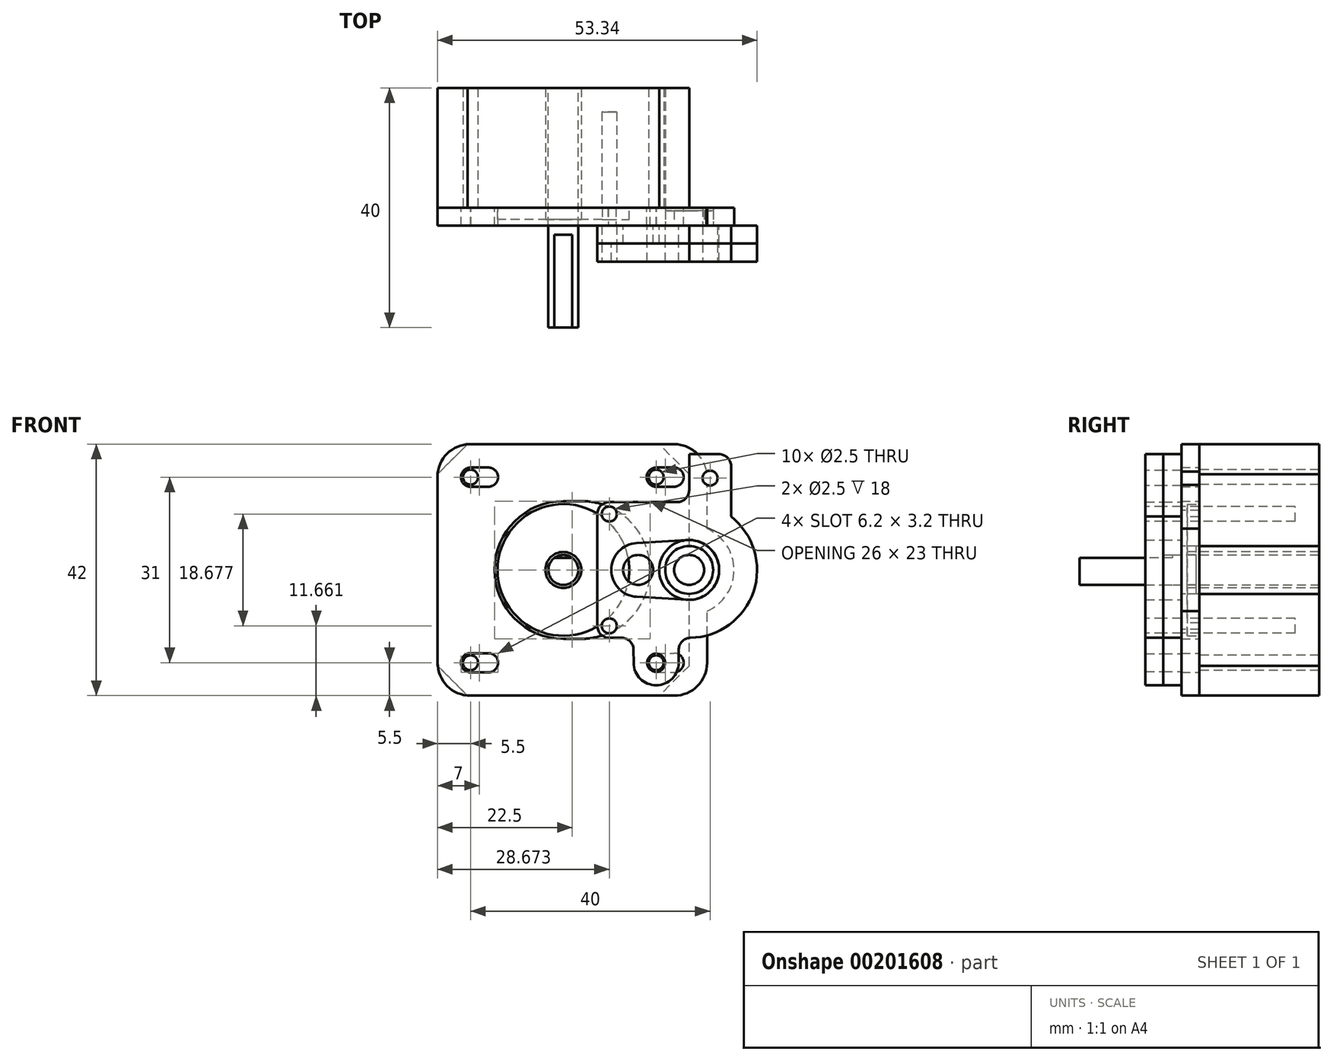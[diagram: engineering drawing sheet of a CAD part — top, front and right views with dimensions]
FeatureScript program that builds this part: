
annotation { "Feature Type Name" : "Feature", "Feature Type Description" : "" }
export const myFeature = defineFeature(function(context is Context, id is Id, definition is map)
    precondition{}
    {
        {
            var Q0;
            Q0=qCreatedBy(makeId("Front.planeOp"),FACE);
            var sketch = newSketch(context, id + "F0", { "sketchPlane" : qUnion([Q0])});
            skCircle(sketch, "E0", {"center": v(0, 0) * mm, "radius": 11 * mm});
            skCircle(sketch, "E1", {"center": v(0, 0) * mm, "radius": 3 * mm});
            skLineSegment(sketch, "E2.bottom", {"start": v(21, -21) * mm, "end": v(-21, -21) * mm});
            skLineSegment(sketch, "E2.top", {"start": v(21, 21) * mm, "end": v(-21, 21) * mm});
            skLineSegment(sketch, "E2.left", {"start": v(21, -21) * mm, "end": v(21, 21) * mm});
            skLineSegment(sketch, "E2.right", {"start": v(-21, -21) * mm, "end": v(-21, 21) * mm});
            skLineSegment(sketch, "E3.bottom", {"start": v(15.5, -15.5) * mm, "end": v(-15.5, -15.5) * mm, "construction": true});
            skLineSegment(sketch, "E3.top", {"start": v(15.5, 15.5) * mm, "end": v(-15.5, 15.5) * mm, "construction": true});
            skLineSegment(sketch, "E3.left", {"start": v(15.5, -15.5) * mm, "end": v(15.5, 15.5) * mm, "construction": true});
            skLineSegment(sketch, "E3.right", {"start": v(-15.5, -15.5) * mm, "end": v(-15.5, 15.5) * mm, "construction": true});
            skCircle(sketch, "E4", {"center": v(-15.5, 15.5) * mm, "radius": 1.25 * mm});
            skCircle(sketch, "E5", {"center": v(15.5, 15.5) * mm, "radius": 1.25 * mm});
            skCircle(sketch, "E6", {"center": v(15.5, -15.5) * mm, "radius": 1.25 * mm});
            skCircle(sketch, "E7", {"center": v(-15.5, -15.5) * mm, "radius": 1.25 * mm});
            skSolve(sketch);
        }
        {
            var Q0;
            Q0 = qSketchRegion(id + "F0", true);
            var Q1;
            Q1=makeQuery(id+"F0.imprint","IMPRINT",FACE,{"disambiguationData":[TD([[makeQuery(id+"F0.imprint","IMPRINT",EDGE,{"derivedFrom":sQuery(id+"F0.wireOp",EDGE,"E0")}),1.0]])]});
            extrude(context, id + "F1", {"entities" : qUnion([Q0, Q1]), "oppositeDirection" : true, "depth" : 20 * mm});
        }
        {
            var Q0;
            Q0=makeQuery(id+"F0.imprint","IMPRINT",FACE,{"disambiguationData":[TD([[makeQuery(id+"F0.imprint","IMPRINT",EDGE,{"derivedFrom":sQuery(id+"F0.wireOp",EDGE,"E0")}),1.0]])]});
            extrude(context, id + "F2", {"entities" : qUnion([Q0]), "operationType" : NewBodyOperationType.ADD, "depth" : 2 * mm});
        }
        {
            var Q0;
            Q0=makeQuery(id+"F1.opExtrude","SWEPT_EDGE",EDGE,{"disambiguationData":[OSD([sQuery(id+"F0.wireOp",EDGE,"E2.top"),sQuery(id+"F0.wireOp",EDGE,"E2.right")])]});
            var Q1;
            Q1=makeQuery(id+"F1.opExtrude","SWEPT_EDGE",EDGE,{"disambiguationData":[OSD([sQuery(id+"F0.wireOp",EDGE,"E2.top"),sQuery(id+"F0.wireOp",EDGE,"E2.left")])]});
            var Q2;
            Q2=makeQuery(id+"F1.opExtrude","SWEPT_EDGE",EDGE,{"disambiguationData":[OSD([sQuery(id+"F0.wireOp",EDGE,"E2.bottom"),sQuery(id+"F0.wireOp",EDGE,"E2.left")])]});
            var Q3;
            Q3=makeQuery(id+"F1.opExtrude","SWEPT_EDGE",EDGE,{"disambiguationData":[OSD([sQuery(id+"F0.wireOp",EDGE,"E2.bottom"),sQuery(id+"F0.wireOp",EDGE,"E2.right")])]});
            chamfer(context, id + "F3", {"entities" : qUnion([Q0, Q1, Q2, Q3]), "width" : 5 * mm, "tangentPropagation" : true});
        }
        {
            var Q0;
            Q0=makeQuery(id+"F1.opExtrude","CAP_FACE",FACE,{"disambiguationData":[OSD([sQuery(id+"F0.wireOp",EDGE,"E1"),sQuery(id+"F0.wireOp",EDGE,"E2.bottom"),sQuery(id+"F0.wireOp",EDGE,"E2.top"),sQuery(id+"F0.wireOp",EDGE,"E2.left"),sQuery(id+"F0.wireOp",EDGE,"E2.right"),sQuery(id+"F0.wireOp",EDGE,"E4"),sQuery(id+"F0.wireOp",EDGE,"E5"),sQuery(id+"F0.wireOp",EDGE,"E6"),sQuery(id+"F0.wireOp",EDGE,"E7")])],"isStart":false});
            var sketch = newSketch(context, id + "F4", { "sketchPlane" : qUnion([Q0])});
            skCircle(sketch, "E8", {"center": v(0, 0) * mm, "radius": 2.5 * mm});
            skSolve(sketch);
        }
        {
            var Q0;
            Q0 = qSketchRegion(id + "F4", true);
            extrude(context, id + "F5", {"entities" : qUnion([Q0]), "oppositeDirection" : true, "depth" : 40 * mm});
        }
        {
            var Q0;
            Q0=makeQuery(id+"F5.opExtrude","CAP_FACE",FACE,{"disambiguationData":[OSD([sQuery(id+"F4.wireOp",EDGE,"E8")])],"isStart":false});
            var sketch = newSketch(context, id + "F6", { "sketchPlane" : qUnion([Q0])});
            skLineSegment(sketch, "E9", {"start": v(-6.96, 2) * mm, "end": v(7.74, 2) * mm});
            skSolve(sketch);
        }
        {
            var Q0;
            {var subQ0=sQuery(id+"F6.wireOp",EDGE,"E9");var subQ1=makeQuery(id+"F5.opExtrude","CAP_EDGE",EDGE,{"disambiguationData":[OSD([sQuery(id+"F4.wireOp",EDGE,"E8")])],"isStart":false});var subQ2=makeQuery(id+"F6.imprint","INTERSECT",VERTEX,{"disambiguationData":[OD(0.0)],"derivedFrom":[subQ1,subQ0]});Q0=makeQuery(id+"F6.imprint","IMPRINT",FACE,{"disambiguationData":[TD([[makeQuery(id+"F6.imprint","IMPRINT",EDGE,{"disambiguationData":[TD([[subQ2,-1.0]])],"derivedFrom":subQ0}),1.0]])]});}
            extrude(context, id + "F7", {"entities" : qUnion([Q0]), "operationType" : NewBodyOperationType.REMOVE, "oppositeDirection" : true, "depth" : 15.5 * mm});
        }
        {
            var Q0;
            Q0=makeQuery(id+"F1.opExtrude","CAP_FACE",FACE,{"disambiguationData":[OSD([sQuery(id+"F0.wireOp",EDGE,"E1"),sQuery(id+"F0.wireOp",EDGE,"E2.bottom"),sQuery(id+"F0.wireOp",EDGE,"E2.top"),sQuery(id+"F0.wireOp",EDGE,"E2.left"),sQuery(id+"F0.wireOp",EDGE,"E2.right"),sQuery(id+"F0.wireOp",EDGE,"E4"),sQuery(id+"F0.wireOp",EDGE,"E5"),sQuery(id+"F0.wireOp",EDGE,"E6"),sQuery(id+"F0.wireOp",EDGE,"E7")])],"isStart":true});
            var sketch = newSketch(context, id + "F8", { "sketchPlane" : qUnion([Q0])});
            skArc(sketch, "E10", {"start": v(-15.48, 17.1) * mm, "mid": v(-17.1, 15.47) * mm, "end": v(-15.41, 13.9) * mm});
            skLineSegment(sketch, "E11", {"start": v(-15.5, 15.5) * mm, "end": v(-10.86, 15.5) * mm, "construction": true});
            skLineSegment(sketch, "E12", {"start": v(0, 0) * mm, "end": v(16.5, 0) * mm, "construction": true});
            skArc(sketch, "E13", {"start": v(-12.5, 13.9) * mm, "mid": v(-10.9, 15.5) * mm, "end": v(-12.5, 17.1) * mm});
            skArc(sketch, "E14", {"start": v(3, -11.5) * mm, "mid": v(14.5, 0) * mm, "end": v(3, 11.5) * mm});
            skLineSegment(sketch, "E15", {"start": v(-15.52, 17.1) * mm, "end": v(-12.5, 17.1) * mm});
            skLineSegment(sketch, "E16", {"start": v(-15.41, 13.9) * mm, "end": v(-12.5, 13.9) * mm});
            skLineSegment(sketch, "E17", {"start": v(0, 11.5) * mm, "end": v(3, 11.5) * mm});
            skLineSegment(sketch, "E18", {"start": v(0, -11.5) * mm, "end": v(3, -11.5) * mm});
            skArc(sketch, "E19.trimOffspring", {"start": v(0, 11.5) * mm, "mid": v(-11.5, 0) * mm, "end": v(0, -11.5) * mm});
            skLineSegment(sketch, "E20.0.1.0", {"start": v(-15.5, -15.5) * mm, "end": v(-10.86, -15.5) * mm, "construction": true});
            skArc(sketch, "E20.0.1.1", {"start": v(-15.48, -13.9) * mm, "mid": v(-17.1, -15.53) * mm, "end": v(-15.41, -17.1) * mm});
            skLineSegment(sketch, "E20.0.1.2", {"start": v(-15.41, -17.1) * mm, "end": v(-12.5, -17.1) * mm});
            skArc(sketch, "E20.0.1.3", {"start": v(-12.5, -17.1) * mm, "mid": v(-10.9, -15.5) * mm, "end": v(-12.5, -13.9) * mm});
            skLineSegment(sketch, "E20.0.1.4", {"start": v(-15.52, -13.9) * mm, "end": v(-12.5, -13.9) * mm});
            skLineSegment(sketch, "E20.1.0.0", {"start": v(15.5, 15.5) * mm, "end": v(20.14, 15.5) * mm, "construction": true});
            skArc(sketch, "E20.1.0.1", {"start": v(15.52, 17.1) * mm, "mid": v(13.9, 15.47) * mm, "end": v(15.59, 13.9) * mm});
            skLineSegment(sketch, "E20.1.0.2", {"start": v(15.59, 13.9) * mm, "end": v(18.5, 13.9) * mm});
            skArc(sketch, "E20.1.0.3", {"start": v(18.5, 13.9) * mm, "mid": v(20.1, 15.5) * mm, "end": v(18.5, 17.1) * mm});
            skLineSegment(sketch, "E20.1.0.4", {"start": v(15.48, 17.1) * mm, "end": v(18.5, 17.1) * mm});
            skLineSegment(sketch, "E20.1.1.0", {"start": v(15.5, -15.5) * mm, "end": v(20.14, -15.5) * mm, "construction": true});
            skArc(sketch, "E20.1.1.1", {"start": v(15.52, -13.9) * mm, "mid": v(13.9, -15.53) * mm, "end": v(15.59, -17.1) * mm});
            skLineSegment(sketch, "E20.1.1.2", {"start": v(15.59, -17.1) * mm, "end": v(18.5, -17.1) * mm});
            skArc(sketch, "E20.1.1.3", {"start": v(18.5, -17.1) * mm, "mid": v(20.1, -15.5) * mm, "end": v(18.5, -13.9) * mm});
            skLineSegment(sketch, "E20.1.1.4", {"start": v(15.48, -13.9) * mm, "end": v(18.5, -13.9) * mm});
            skLineSegment(sketch, "E20.direction1", {"start": v(-15.41, 13.9) * mm, "end": v(15.59, 13.9) * mm, "construction": true});
            skLineSegment(sketch, "E20.direction2", {"start": v(-15.41, 13.9) * mm, "end": v(-15.41, -17.1) * mm, "construction": true});
            skLineSegment(sketch, "E21.bottom", {"start": v(18.5, -21) * mm, "end": v(-15.5, -21) * mm});
            skLineSegment(sketch, "E21.top", {"start": v(18.5, 21) * mm, "end": v(-15.6, 21) * mm});
            skLineSegment(sketch, "E21.left", {"start": v(24, -15.5) * mm, "end": v(24, -6.87) * mm});
            skLineSegment(sketch, "E22", {"start": v(-21, -15.5) * mm, "end": v(-21, 15.6) * mm});
            skPoint(sketch, "E23.orphan", {"position": v(-21, 0) * mm});
            skPoint(sketch, "E21.right.end.orphan", {"position": v(-24, 21) * mm});
            skPoint(sketch, "E21.right.start.orphan", {"position": v(-24, -21) * mm});
            skLineSegment(sketch, "E24.trimOffspring", {"start": v(24, 6.87) * mm, "end": v(24, 15.5) * mm});
            skPoint(sketch, "E25.visualSharp", {"position": v(24, 21) * mm});
            skArc(sketch, "E25.filletArc", {"start": v(24, 15.5) * mm, "mid": v(22.39, 19.39) * mm, "end": v(18.5, 21) * mm});
            skPoint(sketch, "E26.visualSharp", {"position": v(-21, 21) * mm});
            skArc(sketch, "E26.filletArc", {"start": v(-15.6, 21) * mm, "mid": v(-19.42, 19.42) * mm, "end": v(-21, 15.6) * mm});
            skPoint(sketch, "E27.visualSharp", {"position": v(-21, -21) * mm});
            skArc(sketch, "E27.filletArc", {"start": v(-21, -15.5) * mm, "mid": v(-19.39, -19.39) * mm, "end": v(-15.5, -21) * mm});
            skPoint(sketch, "E28.visualSharp", {"position": v(24, -21) * mm});
            skArc(sketch, "E28.filletArc", {"start": v(18.5, -21) * mm, "mid": v(22.39, -19.39) * mm, "end": v(24, -15.5) * mm});
            skArc(sketch, "E29", {"start": v(24, -6.87) * mm, "mid": v(28.5, 0) * mm, "end": v(24, 6.87) * mm});
            skSolve(sketch);
        }
        {
            var Q0;
            Q0 = qSketchRegion(id + "F8", true);
            extrude(context, id + "F9", {"entities" : qUnion([Q0]), "depth" : 3 * mm});
        }
        {
            var Q0;
            Q0=makeQuery(id+"F9.opExtrude","CAP_FACE",FACE,{"disambiguationData":[OSD([sQuery(id+"F8.wireOp",EDGE,"E10"),sQuery(id+"F8.wireOp",EDGE,"E13"),sQuery(id+"F8.wireOp",EDGE,"E14"),sQuery(id+"F8.wireOp",EDGE,"E15"),sQuery(id+"F8.wireOp",EDGE,"E16"),sQuery(id+"F8.wireOp",EDGE,"E17"),sQuery(id+"F8.wireOp",EDGE,"E18"),sQuery(id+"F8.wireOp",EDGE,"E19.trimOffspring"),sQuery(id+"F8.wireOp",EDGE,"E20.0.1.1"),sQuery(id+"F8.wireOp",EDGE,"E20.0.1.2"),sQuery(id+"F8.wireOp",EDGE,"E20.0.1.3"),sQuery(id+"F8.wireOp",EDGE,"E20.0.1.4"),sQuery(id+"F8.wireOp",EDGE,"E20.1.0.1"),sQuery(id+"F8.wireOp",EDGE,"E20.1.0.2"),sQuery(id+"F8.wireOp",EDGE,"E20.1.0.3"),sQuery(id+"F8.wireOp",EDGE,"E20.1.0.4"),sQuery(id+"F8.wireOp",EDGE,"E20.1.1.1"),sQuery(id+"F8.wireOp",EDGE,"E20.1.1.2"),sQuery(id+"F8.wireOp",EDGE,"E20.1.1.3"),sQuery(id+"F8.wireOp",EDGE,"E20.1.1.4"),sQuery(id+"F8.wireOp",EDGE,"E21.bottom"),sQuery(id+"F8.wireOp",EDGE,"E21.top"),sQuery(id+"F8.wireOp",EDGE,"E21.left"),sQuery(id+"F8.wireOp",EDGE,"E22")])],"isStart":false});
            var sketch = newSketch(context, id + "F10", { "sketchPlane" : qUnion([Q0])});
            skPoint(sketch, "E30.endSnap0", {"position": v(24, -11.19) * mm});
            skLineSegment(sketch, "E31", {"start": v(0, 0) * mm, "end": v(21, 0) * mm, "construction": true});
            skCircle(sketch, "E32", {"center": v(21, 0) * mm, "radius": 4 * mm});
            skSolve(sketch);
        }
        {
            var Q0;
            Q0=makeQuery(id+"F10.imprint","IMPRINT",FACE,{"disambiguationData":[TD([[makeQuery(id+"F10.imprint","IMPRINT",EDGE,{"derivedFrom":sQuery(id+"F10.wireOp",EDGE,"E32")}),1.0]])]});
            extrude(context, id + "F11", {"entities" : qUnion([Q0]), "operationType" : NewBodyOperationType.REMOVE, "oppositeDirection" : true, "depth" : 25 * mm});
        }
        {
            var Q0;
            Q0=makeQuery(id+"F9.opExtrude","CAP_FACE",FACE,{"disambiguationData":[OSD([sQuery(id+"F8.wireOp",EDGE,"E10"),sQuery(id+"F8.wireOp",EDGE,"E13"),sQuery(id+"F8.wireOp",EDGE,"E14"),sQuery(id+"F8.wireOp",EDGE,"E15"),sQuery(id+"F8.wireOp",EDGE,"E16"),sQuery(id+"F8.wireOp",EDGE,"E17"),sQuery(id+"F8.wireOp",EDGE,"E18"),sQuery(id+"F8.wireOp",EDGE,"E19.trimOffspring"),sQuery(id+"F8.wireOp",EDGE,"E20.0.1.1"),sQuery(id+"F8.wireOp",EDGE,"E20.0.1.2"),sQuery(id+"F8.wireOp",EDGE,"E20.0.1.3"),sQuery(id+"F8.wireOp",EDGE,"E20.0.1.4"),sQuery(id+"F8.wireOp",EDGE,"E20.1.0.1"),sQuery(id+"F8.wireOp",EDGE,"E20.1.0.2"),sQuery(id+"F8.wireOp",EDGE,"E20.1.0.3"),sQuery(id+"F8.wireOp",EDGE,"E20.1.0.4"),sQuery(id+"F8.wireOp",EDGE,"E20.1.1.1"),sQuery(id+"F8.wireOp",EDGE,"E20.1.1.2"),sQuery(id+"F8.wireOp",EDGE,"E20.1.1.3"),sQuery(id+"F8.wireOp",EDGE,"E20.1.1.4"),sQuery(id+"F8.wireOp",EDGE,"E21.bottom"),sQuery(id+"F8.wireOp",EDGE,"E21.top"),sQuery(id+"F8.wireOp",EDGE,"E21.left"),sQuery(id+"F8.wireOp",EDGE,"E22"),sQuery(id+"F8.wireOp",EDGE,"E24.trimOffspring"),sQuery(id+"F8.wireOp",EDGE,"E25.filletArc"),sQuery(id+"F8.wireOp",EDGE,"E26.filletArc"),sQuery(id+"F8.wireOp",EDGE,"E27.filletArc"),sQuery(id+"F8.wireOp",EDGE,"E28.filletArc"),sQuery(id+"F8.wireOp",EDGE,"E29")])],"isStart":false});
            var sketch = newSketch(context, id + "F12", { "sketchPlane" : qUnion([Q0])});
            skCircle(sketch, "E33", {"center": v(21, 0) * mm, "radius": 4 * mm});
            skCircle(sketch, "E34", {"center": v(21, 0) * mm, "radius": 2.5 * mm});
            skSolve(sketch);
        }
        {
            var Q0;
            Q0=makeQuery(id+"F12.imprint","IMPRINT",FACE,{"disambiguationData":[TD([[makeQuery(id+"F12.imprint","IMPRINT",EDGE,{"derivedFrom":sQuery(id+"F12.wireOp",EDGE,"E33")}),1.0]])]});
            extrude(context, id + "F13", {"entities" : qUnion([Q0]), "oppositeDirection" : true, "depth" : 2.5 * mm});
        }
        {
            var Q0;
            Q0=makeQuery(id+"F9.opExtrude","CAP_FACE",FACE,{"disambiguationData":[OSD([sQuery(id+"F8.wireOp",EDGE,"E10"),sQuery(id+"F8.wireOp",EDGE,"E13"),sQuery(id+"F8.wireOp",EDGE,"E14"),sQuery(id+"F8.wireOp",EDGE,"E15"),sQuery(id+"F8.wireOp",EDGE,"E16"),sQuery(id+"F8.wireOp",EDGE,"E17"),sQuery(id+"F8.wireOp",EDGE,"E18"),sQuery(id+"F8.wireOp",EDGE,"E19.trimOffspring"),sQuery(id+"F8.wireOp",EDGE,"E20.0.1.1"),sQuery(id+"F8.wireOp",EDGE,"E20.0.1.2"),sQuery(id+"F8.wireOp",EDGE,"E20.0.1.3"),sQuery(id+"F8.wireOp",EDGE,"E20.0.1.4"),sQuery(id+"F8.wireOp",EDGE,"E20.1.0.1"),sQuery(id+"F8.wireOp",EDGE,"E20.1.0.2"),sQuery(id+"F8.wireOp",EDGE,"E20.1.0.3"),sQuery(id+"F8.wireOp",EDGE,"E20.1.0.4"),sQuery(id+"F8.wireOp",EDGE,"E20.1.1.1"),sQuery(id+"F8.wireOp",EDGE,"E20.1.1.2"),sQuery(id+"F8.wireOp",EDGE,"E20.1.1.3"),sQuery(id+"F8.wireOp",EDGE,"E20.1.1.4"),sQuery(id+"F8.wireOp",EDGE,"E21.bottom"),sQuery(id+"F8.wireOp",EDGE,"E21.top"),sQuery(id+"F8.wireOp",EDGE,"E21.left"),sQuery(id+"F8.wireOp",EDGE,"E22"),sQuery(id+"F8.wireOp",EDGE,"E24.trimOffspring"),sQuery(id+"F8.wireOp",EDGE,"E25.filletArc"),sQuery(id+"F8.wireOp",EDGE,"E26.filletArc"),sQuery(id+"F8.wireOp",EDGE,"E27.filletArc"),sQuery(id+"F8.wireOp",EDGE,"E28.filletArc"),sQuery(id+"F8.wireOp",EDGE,"E29")])],"isStart":false});
            var sketch = newSketch(context, id + "F14", { "sketchPlane" : qUnion([Q0])});
            skLineSegment(sketch, "E35.right", {"start": v(5.67, -9.34) * mm, "end": v(5.67, 9.34) * mm});
            skPoint(sketch, "E35.middle", {"position": v(21, 0) * mm});
            skLineSegment(sketch, "E36.right", {"start": v(19.26, -15.5) * mm, "end": v(19.26, -13.34) * mm});
            skLineSegment(sketch, "E37.trimOffspring", {"start": v(9.72, -11.34) * mm, "end": v(7.67, -11.34) * mm});
            skPoint(sketch, "E38.visualSharp", {"position": v(19.26, -11.34) * mm});
            skArc(sketch, "E38.filletArc", {"start": v(21.26, -11.34) * mm, "mid": v(19.85, -11.92) * mm, "end": v(19.26, -13.34) * mm});
            skCircle(sketch, "E39", {"center": v(21, 0) * mm, "radius": 5 * mm});
            skPoint(sketch, "E40.visualSharp", {"position": v(5.67, 11.34) * mm});
            skArc(sketch, "E40.filletArc", {"start": v(7.67, 11.34) * mm, "mid": v(6.26, 10.75) * mm, "end": v(5.67, 9.34) * mm});
            skPoint(sketch, "E41.visualSharp", {"position": v(5.67, -11.34) * mm});
            skArc(sketch, "E41.filletArc", {"start": v(5.67, -9.34) * mm, "mid": v(6.26, -10.75) * mm, "end": v(7.67, -11.34) * mm});
            skLineSegment(sketch, "E42.top", {"start": v(21, 19.34) * mm, "end": v(26, 19.34) * mm});
            skLineSegment(sketch, "E42.left", {"start": v(21, 13.34) * mm, "end": v(21, 19.34) * mm});
            skLineSegment(sketch, "E42.right", {"start": v(28, 8.92) * mm, "end": v(28, 17.34) * mm});
            skPoint(sketch, "E43.visualSharp", {"position": v(28, 19.34) * mm});
            skArc(sketch, "E43.filletArc", {"start": v(28, 17.34) * mm, "mid": v(27.41, 18.75) * mm, "end": v(26, 19.34) * mm});
            skLineSegment(sketch, "E44.trimOffspring", {"start": v(19, 11.34) * mm, "end": v(7.67, 11.34) * mm});
            skPoint(sketch, "E45.visualSharp", {"position": v(21, 11.34) * mm});
            skArc(sketch, "E45.filletArc", {"start": v(19, 11.34) * mm, "mid": v(20.41, 11.92) * mm, "end": v(21, 13.34) * mm});
            skArc(sketch, "E46", {"start": v(21.18, -11.34) * mm, "mid": v(31.75, -3.62) * mm, "end": v(28, 8.92) * mm});
            skPoint(sketch, "E35.left.end.orphan", {"position": v(36.33, 11.34) * mm});
            skPoint(sketch, "E35.left.start.orphan", {"position": v(36.33, -11.34) * mm});
            skCircle(sketch, "E47", {"center": v(12.5, 0) * mm, "radius": 4 * mm, "construction": true});
            skCircle(sketch, "E48", {"center": v(12.5, 0) * mm, "radius": 2.5 * mm});
            skArc(sketch, "E49", {"start": v(11.74, -15.53) * mm, "mid": v(15.52, -19.26) * mm, "end": v(19.26, -15.5) * mm});
            skLineSegment(sketch, "E50", {"start": v(11.74, -15.53) * mm, "end": v(11.72, -13.32) * mm});
            skPoint(sketch, "E50.startSnap0", {"position": v(13.9, -15.53) * mm});
            skArc(sketch, "E51.filletArc", {"start": v(11.72, -13.32) * mm, "mid": v(11.13, -11.92) * mm, "end": v(9.72, -11.34) * mm});
            skCircle(sketch, "E52", {"center": v(15.5, -15.5) * mm, "radius": 1.5 * mm});
            skSolve(sketch);
        }
        {
            var Q0;
            Q0 = qSketchRegion(id + "F14", true);
            extrude(context, id + "F15", {"entities" : qUnion([Q0]), "depth" : 3 * mm});
        }
        {
            var Q0;
            Q0=makeQuery(id+"F15.opExtrude","CAP_FACE",FACE,{"disambiguationData":[OSD([sQuery(id+"F14.wireOp",EDGE,"E35.right"),sQuery(id+"F14.wireOp",EDGE,"E36.right"),sQuery(id+"F14.wireOp",EDGE,"E37.trimOffspring"),sQuery(id+"F14.wireOp",EDGE,"E38.filletArc"),sQuery(id+"F14.wireOp",EDGE,"E39"),sQuery(id+"F14.wireOp",EDGE,"E40.filletArc"),sQuery(id+"F14.wireOp",EDGE,"E41.filletArc"),sQuery(id+"F14.wireOp",EDGE,"E42.top"),sQuery(id+"F14.wireOp",EDGE,"E42.left"),sQuery(id+"F14.wireOp",EDGE,"E42.right"),sQuery(id+"F14.wireOp",EDGE,"E43.filletArc"),sQuery(id+"F14.wireOp",EDGE,"E44.trimOffspring"),sQuery(id+"F14.wireOp",EDGE,"E45.filletArc"),sQuery(id+"F14.wireOp",EDGE,"E46"),sQuery(id+"F14.wireOp",EDGE,"E48"),sQuery(id+"F14.wireOp",EDGE,"E49"),sQuery(id+"F14.wireOp",EDGE,"E50"),sQuery(id+"F14.wireOp",EDGE,"E51.filletArc"),sQuery(id+"F14.wireOp",EDGE,"E52")])],"isStart":false});
            var sketch = newSketch(context, id + "F16", { "sketchPlane" : qUnion([Q0])});
            skArc(sketch, "E53.0.0", {"start": v(21.18, -11.34) * mm, "mid": v(31.75, -3.62) * mm, "end": v(28, 8.92) * mm});
            skLineSegment(sketch, "E53.0.1", {"start": v(28, 8.92) * mm, "end": v(28, 17.34) * mm});
            skArc(sketch, "E53.0.2", {"start": v(28, 17.34) * mm, "mid": v(27.41, 18.75) * mm, "end": v(26, 19.34) * mm});
            skLineSegment(sketch, "E53.0.3", {"start": v(26, 19.34) * mm, "end": v(21, 19.34) * mm});
            skLineSegment(sketch, "E53.0.4", {"start": v(21, 19.34) * mm, "end": v(21, 13.34) * mm});
            skArc(sketch, "E53.0.5", {"start": v(21, 13.34) * mm, "mid": v(20.41, 11.92) * mm, "end": v(19, 11.34) * mm});
            skLineSegment(sketch, "E53.0.6", {"start": v(19, 11.34) * mm, "end": v(7.67, 11.34) * mm});
            skArc(sketch, "E53.0.7", {"start": v(7.67, 11.34) * mm, "mid": v(6.26, 10.75) * mm, "end": v(5.67, 9.34) * mm});
            skLineSegment(sketch, "E53.0.8", {"start": v(5.67, 9.34) * mm, "end": v(5.67, -9.34) * mm});
            skArc(sketch, "E53.0.9", {"start": v(5.67, -9.34) * mm, "mid": v(6.26, -10.75) * mm, "end": v(7.67, -11.34) * mm});
            skLineSegment(sketch, "E53.0.10", {"start": v(7.67, -11.34) * mm, "end": v(9.72, -11.34) * mm});
            skArc(sketch, "E53.0.11", {"start": v(9.72, -11.34) * mm, "mid": v(11.13, -11.92) * mm, "end": v(11.72, -13.32) * mm});
            skLineSegment(sketch, "E53.0.12", {"start": v(11.72, -13.32) * mm, "end": v(11.74, -15.53) * mm});
            skArc(sketch, "E53.0.13", {"start": v(11.74, -15.53) * mm, "mid": v(15.52, -19.26) * mm, "end": v(19.26, -15.5) * mm});
            skLineSegment(sketch, "E53.0.14", {"start": v(19.26, -15.5) * mm, "end": v(19.26, -13.34) * mm});
            skArc(sketch, "E53.0.15", {"start": v(19.26, -13.34) * mm, "mid": v(19.82, -11.95) * mm, "end": v(21.18, -11.34) * mm});
            skArc(sketch, "E54.0", {"start": v(20.7, -5) * mm, "mid": v(26, 0) * mm, "end": v(20.7, 5) * mm});
            skCircle(sketch, "E55.0", {"center": v(12.5, 0) * mm, "radius": 2.5 * mm});
            skArc(sketch, "E56", {"start": v(12.24, 4.5) * mm, "mid": v(8, 0) * mm, "end": v(12.24, -4.5) * mm});
            skCircle(sketch, "E57", {"center": v(15.5, -15.5) * mm, "radius": 1.5 * mm});
            skLineSegment(sketch, "E58", {"start": v(12.24, 4.5) * mm, "end": v(20.7, 5) * mm});
            skLineSegment(sketch, "E59", {"start": v(20.7, -5) * mm, "end": v(12.24, -4.5) * mm});
            skSolve(sketch);
        }
        {
            var Q0;
            Q0 = qSketchRegion(id + "F16", true);
            extrude(context, id + "F17", {"entities" : qUnion([Q0]), "depth" : 3 * mm});
        }
        {
            var Q0;
            Q0=makeQuery(id+"F17.opExtrude","CAP_FACE",FACE,{"disambiguationData":[OSD([sQuery(id+"F16.wireOp",EDGE,"E53.0.0"),sQuery(id+"F16.wireOp",EDGE,"E53.0.1"),sQuery(id+"F16.wireOp",EDGE,"E53.0.2"),sQuery(id+"F16.wireOp",EDGE,"E53.0.3"),sQuery(id+"F16.wireOp",EDGE,"E53.0.4"),sQuery(id+"F16.wireOp",EDGE,"E53.0.5"),sQuery(id+"F16.wireOp",EDGE,"E53.0.6"),sQuery(id+"F16.wireOp",EDGE,"E53.0.7"),sQuery(id+"F16.wireOp",EDGE,"E53.0.8"),sQuery(id+"F16.wireOp",EDGE,"E53.0.9"),sQuery(id+"F16.wireOp",EDGE,"E53.0.10"),sQuery(id+"F16.wireOp",EDGE,"E53.0.11"),sQuery(id+"F16.wireOp",EDGE,"E53.0.12"),sQuery(id+"F16.wireOp",EDGE,"E53.0.13"),sQuery(id+"F16.wireOp",EDGE,"E53.0.14"),sQuery(id+"F16.wireOp",EDGE,"E53.0.15"),sQuery(id+"F16.wireOp",EDGE,"E54.0"),sQuery(id+"F16.wireOp",EDGE,"E56"),sQuery(id+"F16.wireOp",EDGE,"E57"),sQuery(id+"F16.wireOp",EDGE,"E58"),sQuery(id+"F16.wireOp",EDGE,"E59")])],"isStart":false});
            var sketch = newSketch(context, id + "F18", { "sketchPlane" : qUnion([Q0])});
            skLineSegment(sketch, "E60", {"start": v(28.4, 15.34) * mm, "end": v(11.65, 15.34) * mm, "construction": true});
            skLineSegment(sketch, "E61", {"start": v(24.5, 11.9) * mm, "end": v(24.5, 22.87) * mm, "construction": true});
            skCircle(sketch, "E62", {"center": v(24.5, 15.34) * mm, "radius": 1.25 * mm});
            skCircle(sketch, "E63", {"center": v(7.67, -9.34) * mm, "radius": 1.25 * mm});
            skCircle(sketch, "E64", {"center": v(7.67, 9.34) * mm, "radius": 1.25 * mm});
            skSolve(sketch);
        }
        {
            var Q0;
            Q0=makeQuery(id+"F18.imprint","IMPRINT",FACE,{"disambiguationData":[TD([[makeQuery(id+"F18.imprint","IMPRINT",EDGE,{"derivedFrom":sQuery(id+"F18.wireOp",EDGE,"E62")}),1.0]])]});
            var Q1;
            Q1=makeQuery(id+"F18.imprint","IMPRINT",FACE,{"disambiguationData":[TD([[makeQuery(id+"F18.imprint","IMPRINT",EDGE,{"derivedFrom":sQuery(id+"F18.wireOp",EDGE,"E64")}),1.0]])]});
            var Q2;
            Q2=makeQuery(id+"F18.imprint","IMPRINT",FACE,{"disambiguationData":[TD([[makeQuery(id+"F18.imprint","IMPRINT",EDGE,{"derivedFrom":sQuery(id+"F18.wireOp",EDGE,"E63")}),1.0]])]});
            extrude(context, id + "F19", {"entities" : qUnion([Q0, Q1, Q2]), "operationType" : NewBodyOperationType.REMOVE, "oppositeDirection" : true, "depth" : 25 * mm});
        }
    });
